# Revit family: QF_BOURGEAT_Conteneurs_Isothermes_GN_ouverture_Frontale
name_source: partatom
category: Equipement spécialisé
revit_build: Autodesk Revit 2015 (Build: 20140606_1530(x64)
units: mm (PartAtom-declared; Revit-internal decimal feet)

## types (7) — shared parameters
Certification = NF Hygiene alimentaire
Conception = En polyéthylène alimentaire
Fabricant = BOURGEAT
Longueur hors tout = 478 mm  [stored 1.56824 ft]
Nature isolant = Mousse sans PU
Spécification du Fabricant = Conteneur isotherme
URL catalogue = http://www.bourgeat.fr
zero-valued in all types: Puissance frigorifique

## per-type parameters (varying)
| type | 2 poignées | 4 poignées | Charge max | Fréquence | Hauteur hors tout | Indice de protection | Intensité nominale | Modèle | Phase | Poids net à vide | Profondeur hors tout | Puissance électrique  | Roues | Tension | connecteur | façade |
| F2 Neutre | Oui | Non | 40.00 kg | 0 Hz | 378 mm  [stored 1.24016 ft] |  | 0 A | 821801 | 0 | 11.00 kg | 695 mm  [stored 2.28018 ft] | 0 W | Non | 0 V | Non | Non |
| F3 Neutre | Non | Oui | 50.00 kg | 0 Hz | 534 mm  [stored 1.75197 ft] |  | 0 A | 821901 | 0 | 14.00 kg | 683 mm  [stored 2.24081 ft] | 0 W | Non | 0 V | Non | Oui |
| F4 Neutre | Non | Oui | 60.00 kg | 0 Hz | 632 mm |  | 0 A | 822101 | 0 | 17.00 kg | 683 mm  [stored 2.24081 ft] | 0 W | Non | 0 V | Non | Oui |
| FC3 Chauffant | Non | Oui | 50.00 kg | 50 Hz | 534 mm  [stored 1.75197 ft] | 24 | 1 A | 822000 | 2 | 18.00 kg | 709 mm  [stored 2.32612 ft] | 300 W | Non | 230 V | Oui | Oui |
| FC4 Chauffant | Non | Oui | 60.00 kg | 50 Hz | 632 mm | 24 | 1 A | 822500 | 2 | 17.00 kg | 709 mm  [stored 2.32612 ft] | 300 W | Non | 230 V | Oui | Oui |
| F4 Neutre + Roues | Non | Oui | 60.00 kg | 0 Hz | 632 mm |  | 0 A | 822101 + 822751 | 0 | 17.00 kg | 683 mm  [stored 2.24081 ft] | 0 W | Non | 0 V | Non | Oui |
| FC4 Chauffant + Roues | Non | Oui | 60.00 kg | 50 Hz | 632 mm | 24 | 1 A | 822500 + 822751 | 2 | 17.00 kg | 709 mm  [stored 2.32612 ft] | 300 W | Oui | 230 V | Oui | Oui |

note: [stored X ft] marks values corroborated as IEEE doubles in the binary element streams (Revit-internal decimal feet)
